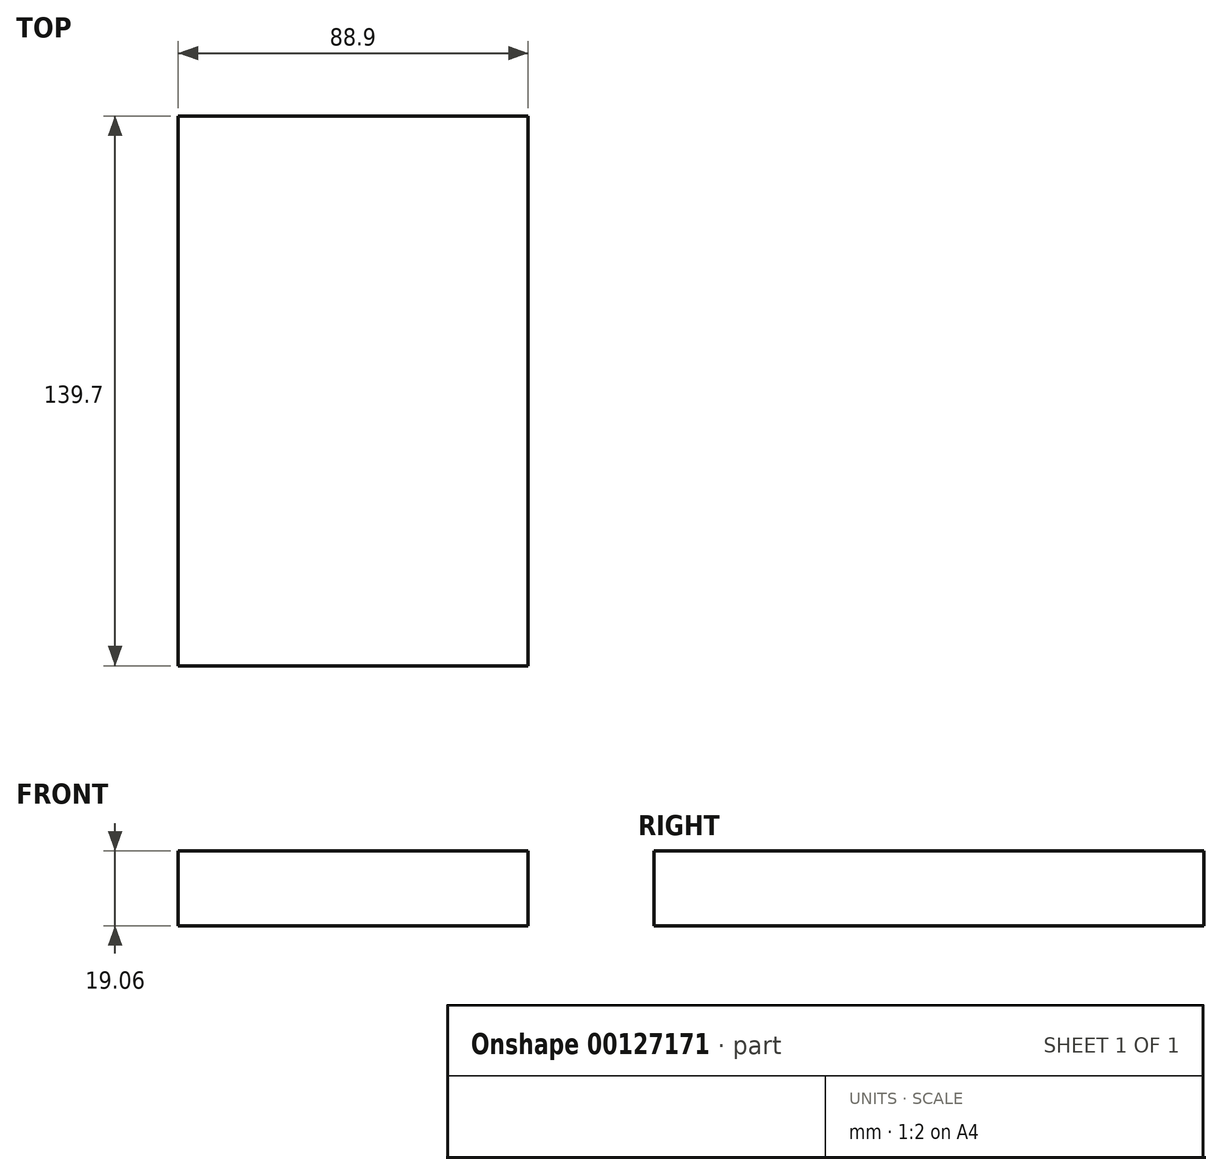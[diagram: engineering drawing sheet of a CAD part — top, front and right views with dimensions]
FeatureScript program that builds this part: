
annotation { "Feature Type Name" : "Feature", "Feature Type Description" : "" }
export const myFeature = defineFeature(function(context is Context, id is Id, definition is map)
    precondition{}
    {
        {
            var Q0;
            Q0=qCreatedBy(makeId("Front.planeOp"),FACE);
            var sketch = newSketch(context, id + "F0", { "sketchPlane" : qUnion([Q0])});
            skLineSegment(sketch, "E0.bottom", {"start": v(44.45, -9.52) * mm, "end": v(-44.45, -9.53) * mm});
            skLineSegment(sketch, "E0.top", {"start": v(44.45, 9.53) * mm, "end": v(-44.45, 9.53) * mm});
            skLineSegment(sketch, "E0.left", {"start": v(44.45, -9.52) * mm, "end": v(44.45, 9.53) * mm});
            skLineSegment(sketch, "E0.right", {"start": v(-44.45, -9.53) * mm, "end": v(-44.45, 9.53) * mm});
            skPoint(sketch, "E0.middle", {"position": v(0, 0) * mm});
            skSolve(sketch);
        }
        {
            var Q0;
            Q0=qSketchRegion(id+"F0",true);
            extrude(context, id + "F1", {"entities" : qUnion([Q0]), "depth" : 139.7 * mm});
        }
    });
